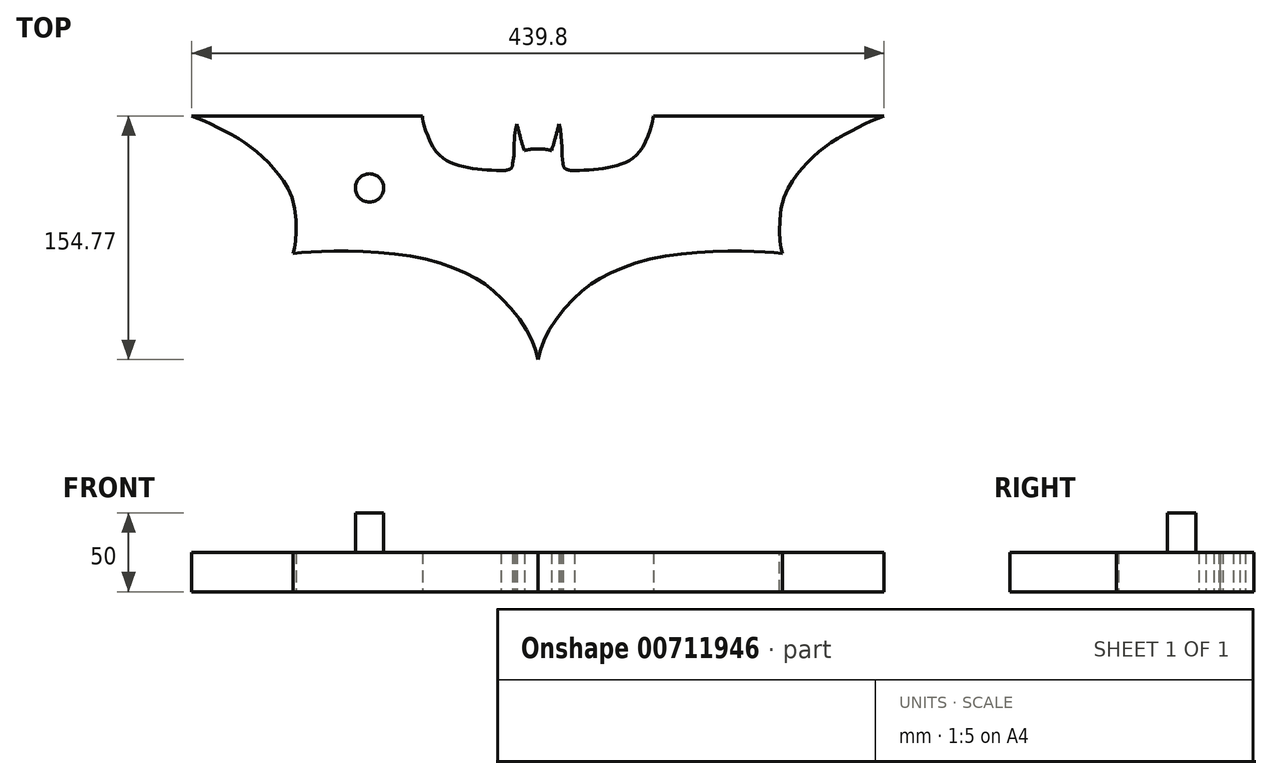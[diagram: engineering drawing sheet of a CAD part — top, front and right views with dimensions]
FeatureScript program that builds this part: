
annotation { "Feature Type Name" : "Feature", "Feature Type Description" : "" }
export const myFeature = defineFeature(function(context is Context, id is Id, definition is map)
    precondition{}
    {
        {
            var Q0;
            Q0=qCreatedBy(makeId("Top.planeOp"),FACE);
            var sketch = newSketch(context, id + "F0", { "sketchPlane" : qUnion([Q0])});
            skFitSpline(sketch, "E0", {"points": [v(0, 55.85) * mm, v(-4.28, 55.8) * mm, v(-8.58, 54.97) * mm], "startDerivative": vector(-8.62, 0.3) * mm, "endDerivative": vector(-8.53, -2.06) * mm});
            skFitSpline(sketch, "E1", {"points": [v(-8.58, 54.97) * mm, v(-10.85, 62.26) * mm, v(-13.35, 71.7) * mm], "startDerivative": vector(-6.87, 17.56) * mm, "endDerivative": vector(-4.7, 18.37) * mm});
            skLineSegment(sketch, "E2", {"start": v(-13.35, 71.7) * mm, "end": v(-14.31, 68.19) * mm});
            skLineSegment(sketch, "E3", {"start": v(-14.31, 68.19) * mm, "end": v(-14.7, 64.22) * mm});
            skLineSegment(sketch, "E4", {"start": v(-14.7, 64.22) * mm, "end": v(-15.24, 57.25) * mm});
            skLineSegment(sketch, "E5", {"start": v(-15.24, 57.25) * mm, "end": v(-15.24, 51.8) * mm});
            skLineSegment(sketch, "E6", {"start": v(-15.24, 51.8) * mm, "end": v(-16.04, 46.55) * mm});
            skFitSpline(sketch, "E7", {"points": [v(-16.04, 46.55) * mm, v(-16.3, 44.84) * mm, v(-17.56, 43.3) * mm, v(-21.49, 42.2) * mm, v(-23.28, 42.12) * mm], "startDerivative": vector(-0.5, -8.1) * mm, "endDerivative": vector(-6.98, 0.05) * mm});
            skFitSpline(sketch, "E8", {"points": [v(-23.28, 42.12) * mm, v(-35.36, 42.9) * mm, v(-47.32, 44.77) * mm, v(-57.36, 48.3) * mm, v(-65.89, 56.08) * mm, v(-72.46, 71.79) * mm, v(-73.38, 77.02) * mm], "startDerivative": vector(-69.4, 3.25) * mm, "endDerivative": vector(-4.27, 38.02) * mm});
            skLineSegment(sketch, "E9", {"start": v(-73.38, 77.02) * mm, "end": v(-219.9, 77.02) * mm});
            skFitSpline(sketch, "E10", {"points": [v(-219.9, 77.02) * mm, v(-210.5, 73.13) * mm, v(-200.84, 68.4) * mm, v(-189.9, 62.45) * mm, v(-180.61, 55.9) * mm, v(-171, 47.18) * mm, v(-163.08, 37.74) * mm, v(-155.24, 21.67) * mm, v(-153.84, -2.63) * mm, v(-155.34, -10.36) * mm], "startDerivative": vector(96.12, -38.16) * mm, "endDerivative": vector(-19.97, -73.82) * mm});
            skFitSpline(sketch, "E11", {"points": [v(-155.34, -10.36) * mm, v(-141.44, -9.39) * mm, v(-111.32, -9.15) * mm, v(-69.35, -14.52) * mm, v(-40.72, -25.63) * mm, v(-24.19, -37.72) * mm, v(-6.28, -60.52) * mm, v(0, -77.75) * mm], "startDerivative": vector(120.68, 9.89) * mm, "endDerivative": vector(36.3, -137.27) * mm});
            skLineSegment(sketch, "E12", {"start": v(0, 88.7) * mm, "end": v(0, -109.34) * mm, "construction": true});
            skLineSegment(sketch, "E13.MirrorCS", {"start": v(15.24, 57.25) * mm, "end": v(15.24, 51.8) * mm});
            skLineSegment(sketch, "E14.MirrorCS", {"start": v(14.7, 64.22) * mm, "end": v(15.24, 57.25) * mm});
            skLineSegment(sketch, "E15.MirrorCS", {"start": v(14.31, 68.19) * mm, "end": v(14.7, 64.22) * mm});
            skLineSegment(sketch, "E16.MirrorCS", {"start": v(13.35, 71.7) * mm, "end": v(14.31, 68.19) * mm});
            skFitSpline(sketch, "E17.MirrorCS", {"points": [v(8.58, 54.97) * mm, v(10.85, 62.26) * mm, v(13.35, 71.7) * mm], "startDerivative": vector(6.87, 17.56) * mm, "endDerivative": vector(4.7, 18.37) * mm});
            skFitSpline(sketch, "E18.MirrorCS", {"points": [v(0, 55.85) * mm, v(4.28, 55.8) * mm, v(8.58, 54.97) * mm], "startDerivative": vector(8.62, 0.3) * mm, "endDerivative": vector(8.53, -2.06) * mm});
            skFitSpline(sketch, "E19.MirrorCS", {"points": [v(16.04, 46.55) * mm, v(16.3, 44.84) * mm, v(17.56, 43.3) * mm, v(21.49, 42.2) * mm, v(23.28, 42.12) * mm], "startDerivative": vector(0.5, -8.1) * mm, "endDerivative": vector(6.98, 0.05) * mm});
            skLineSegment(sketch, "E20.MirrorCS", {"start": v(73.38, 77.02) * mm, "end": v(219.9, 77.02) * mm});
            skLineSegment(sketch, "E21.MirrorCS", {"start": v(15.24, 51.8) * mm, "end": v(16.04, 46.55) * mm});
            skFitSpline(sketch, "E22.MirrorCS", {"points": [v(23.28, 42.12) * mm, v(35.36, 42.9) * mm, v(47.32, 44.77) * mm, v(57.36, 48.3) * mm, v(65.89, 56.08) * mm, v(72.46, 71.79) * mm, v(73.38, 77.02) * mm], "startDerivative": vector(69.4, 3.25) * mm, "endDerivative": vector(4.27, 38.02) * mm});
            skFitSpline(sketch, "E23.MirrorCS", {"points": [v(219.9, 77.02) * mm, v(210.5, 73.13) * mm, v(200.84, 68.4) * mm, v(189.9, 62.45) * mm, v(180.61, 55.9) * mm, v(171, 47.18) * mm, v(163.08, 37.74) * mm, v(155.24, 21.67) * mm, v(153.84, -2.63) * mm, v(155.34, -10.36) * mm], "startDerivative": vector(-96.12, -38.16) * mm, "endDerivative": vector(19.97, -73.82) * mm});
            skFitSpline(sketch, "E24.MirrorCS", {"points": [v(155.34, -10.36) * mm, v(141.44, -9.39) * mm, v(111.32, -9.15) * mm, v(69.35, -14.52) * mm, v(40.72, -25.63) * mm, v(24.19, -37.72) * mm, v(6.28, -60.52) * mm, v(0, -77.75) * mm], "startDerivative": vector(-120.68, 9.89) * mm, "endDerivative": vector(-36.3, -137.27) * mm});
            skLineSegment(sketch, "E25.bottom", {"start": v(-162.66, -64.97) * mm, "end": v(-188.06, -64.97) * mm});
            skLineSegment(sketch, "E25.top", {"start": v(-162.66, -39.57) * mm, "end": v(-188.06, -39.57) * mm});
            skLineSegment(sketch, "E25.left", {"start": v(-162.66, -64.97) * mm, "end": v(-162.66, -39.57) * mm});
            skLineSegment(sketch, "E25.right", {"start": v(-188.06, -64.97) * mm, "end": v(-188.06, -39.57) * mm});
            skPoint(sketch, "E25.middle", {"position": v(-175.36, -52.97) * mm});
            skArc(sketch, "E26", {"start": v(-177.86, -48.64) * mm, "mid": v(-175.36, -57.97) * mm, "end": v(-172.86, -48.64) * mm});
            skArc(sketch, "E27", {"start": v(-172.86, -45.97) * mm, "mid": v(-175.36, -43.47) * mm, "end": v(-177.86, -45.97) * mm});
            skLineSegment(sketch, "E28", {"start": v(-177.86, -45.97) * mm, "end": v(-177.86, -48.64) * mm});
            skLineSegment(sketch, "E29", {"start": v(-172.86, -45.97) * mm, "end": v(-172.86, -48.64) * mm});
            skLineSegment(sketch, "E30.bottom", {"start": v(-135.2, -64.97) * mm, "end": v(-120.2, -64.97) * mm});
            skLineSegment(sketch, "E30.top", {"start": v(-135.2, -39.57) * mm, "end": v(-120.2, -39.57) * mm});
            skLineSegment(sketch, "E30.left", {"start": v(-135.2, -64.97) * mm, "end": v(-135.2, -39.57) * mm});
            skLineSegment(sketch, "E30.right", {"start": v(-120.2, -64.97) * mm, "end": v(-120.2, -39.57) * mm});
            skLineSegment(sketch, "E31.bottom", {"start": v(-111.8, -65.28) * mm, "end": v(-96.8, -65.28) * mm});
            skLineSegment(sketch, "E31.top", {"start": v(-111.8, -39.88) * mm, "end": v(-96.8, -39.88) * mm});
            skLineSegment(sketch, "E31.left", {"start": v(-111.8, -65.28) * mm, "end": v(-111.8, -39.88) * mm});
            skLineSegment(sketch, "E31.right", {"start": v(-96.8, -65.28) * mm, "end": v(-96.8, -39.88) * mm});
            skLineSegment(sketch, "E32.bottom", {"start": v(88.2, -63.98) * mm, "end": v(62.8, -63.98) * mm});
            skLineSegment(sketch, "E32.top", {"start": v(88.2, -38.58) * mm, "end": v(62.8, -38.58) * mm});
            skLineSegment(sketch, "E32.left", {"start": v(88.2, -63.98) * mm, "end": v(88.2, -38.58) * mm});
            skLineSegment(sketch, "E32.right", {"start": v(62.8, -63.98) * mm, "end": v(62.8, -38.58) * mm});
            skPoint(sketch, "E32.middle", {"position": v(75.5, -51.98) * mm});
            skArc(sketch, "E33", {"start": v(73, -47.65) * mm, "mid": v(75.5, -56.98) * mm, "end": v(78, -47.65) * mm});
            skArc(sketch, "E34", {"start": v(78, -44.98) * mm, "mid": v(75.5, -42.48) * mm, "end": v(73, -44.98) * mm});
            skLineSegment(sketch, "E35", {"start": v(73, -44.98) * mm, "end": v(73, -47.65) * mm});
            skLineSegment(sketch, "E36", {"start": v(78, -44.98) * mm, "end": v(78, -47.65) * mm});
            skLineSegment(sketch, "E37.bottom", {"start": v(115.66, -63.98) * mm, "end": v(130.66, -63.98) * mm});
            skLineSegment(sketch, "E37.top", {"start": v(115.66, -38.58) * mm, "end": v(130.66, -38.58) * mm});
            skLineSegment(sketch, "E37.left", {"start": v(115.66, -63.98) * mm, "end": v(115.66, -38.58) * mm});
            skLineSegment(sketch, "E37.right", {"start": v(130.66, -63.98) * mm, "end": v(130.66, -38.58) * mm});
            skLineSegment(sketch, "E38.bottom", {"start": v(139.05, -64.3) * mm, "end": v(154.05, -64.3) * mm});
            skLineSegment(sketch, "E38.top", {"start": v(139.05, -38.9) * mm, "end": v(154.05, -38.9) * mm});
            skLineSegment(sketch, "E38.left", {"start": v(139.05, -64.3) * mm, "end": v(139.05, -38.9) * mm});
            skLineSegment(sketch, "E38.right", {"start": v(154.05, -64.3) * mm, "end": v(154.05, -38.9) * mm});
            skSolve(sketch);
        }
        {
            var Q0;
            Q0=makeQuery(id+"F0.imprint","IMPRINT",FACE,{"disambiguationData":[TD([[makeQuery(id+"F0.imprint","IMPRINT",EDGE,{"derivedFrom":sQuery(id+"F0.wireOp",EDGE,"E0")}),1.0]])]});
            extrude(context, id + "F1", {"entities" : qUnion([Q0]), "depth" : 25 * mm, "offsetDistance" : 25 * mm});
        }
        {
            var Q0;
            Q0=makeQuery(id+"F1.opExtrude","CAP_FACE",FACE,{"disambiguationData":[OSD([sQuery(id+"F0.wireOp",EDGE,"E0"),sQuery(id+"F0.wireOp",EDGE,"E1"),sQuery(id+"F0.wireOp",EDGE,"E2"),sQuery(id+"F0.wireOp",EDGE,"E3"),sQuery(id+"F0.wireOp",EDGE,"E4"),sQuery(id+"F0.wireOp",EDGE,"E5"),sQuery(id+"F0.wireOp",EDGE,"E6"),sQuery(id+"F0.wireOp",EDGE,"E7"),sQuery(id+"F0.wireOp",EDGE,"E8"),sQuery(id+"F0.wireOp",EDGE,"E9"),sQuery(id+"F0.wireOp",EDGE,"E10"),sQuery(id+"F0.wireOp",EDGE,"E11"),sQuery(id+"F0.wireOp",EDGE,"E13.MirrorCS"),sQuery(id+"F0.wireOp",EDGE,"E14.MirrorCS"),sQuery(id+"F0.wireOp",EDGE,"E15.MirrorCS"),sQuery(id+"F0.wireOp",EDGE,"E16.MirrorCS"),sQuery(id+"F0.wireOp",EDGE,"E17.MirrorCS"),sQuery(id+"F0.wireOp",EDGE,"E18.MirrorCS"),sQuery(id+"F0.wireOp",EDGE,"E19.MirrorCS"),sQuery(id+"F0.wireOp",EDGE,"E20.MirrorCS"),sQuery(id+"F0.wireOp",EDGE,"E21.MirrorCS"),sQuery(id+"F0.wireOp",EDGE,"E22.MirrorCS"),sQuery(id+"F0.wireOp",EDGE,"E23.MirrorCS"),sQuery(id+"F0.wireOp",EDGE,"E24.MirrorCS")])],"isStart":false});
            var sketch = newSketch(context, id + "F2", { "sketchPlane" : qUnion([Q0])});
            skCircle(sketch, "E39", {"center": v(-106.92, 31.22) * mm, "radius": 9 * mm});
            skSolve(sketch);
        }
        {
            var Q0;
            Q0=makeQuery(id+"F2.imprint","IMPRINT",FACE,{"disambiguationData":[TD([[makeQuery(id+"F2.imprint","IMPRINT",EDGE,{"derivedFrom":sQuery(id+"F2.wireOp",EDGE,"E39")}),1.0]])]});
            extrude(context, id + "F3", {"entities" : qUnion([Q0]), "operationType" : NewBodyOperationType.ADD, "depth" : 25 * mm, "offsetDistance" : 25 * mm});
        }
    });
